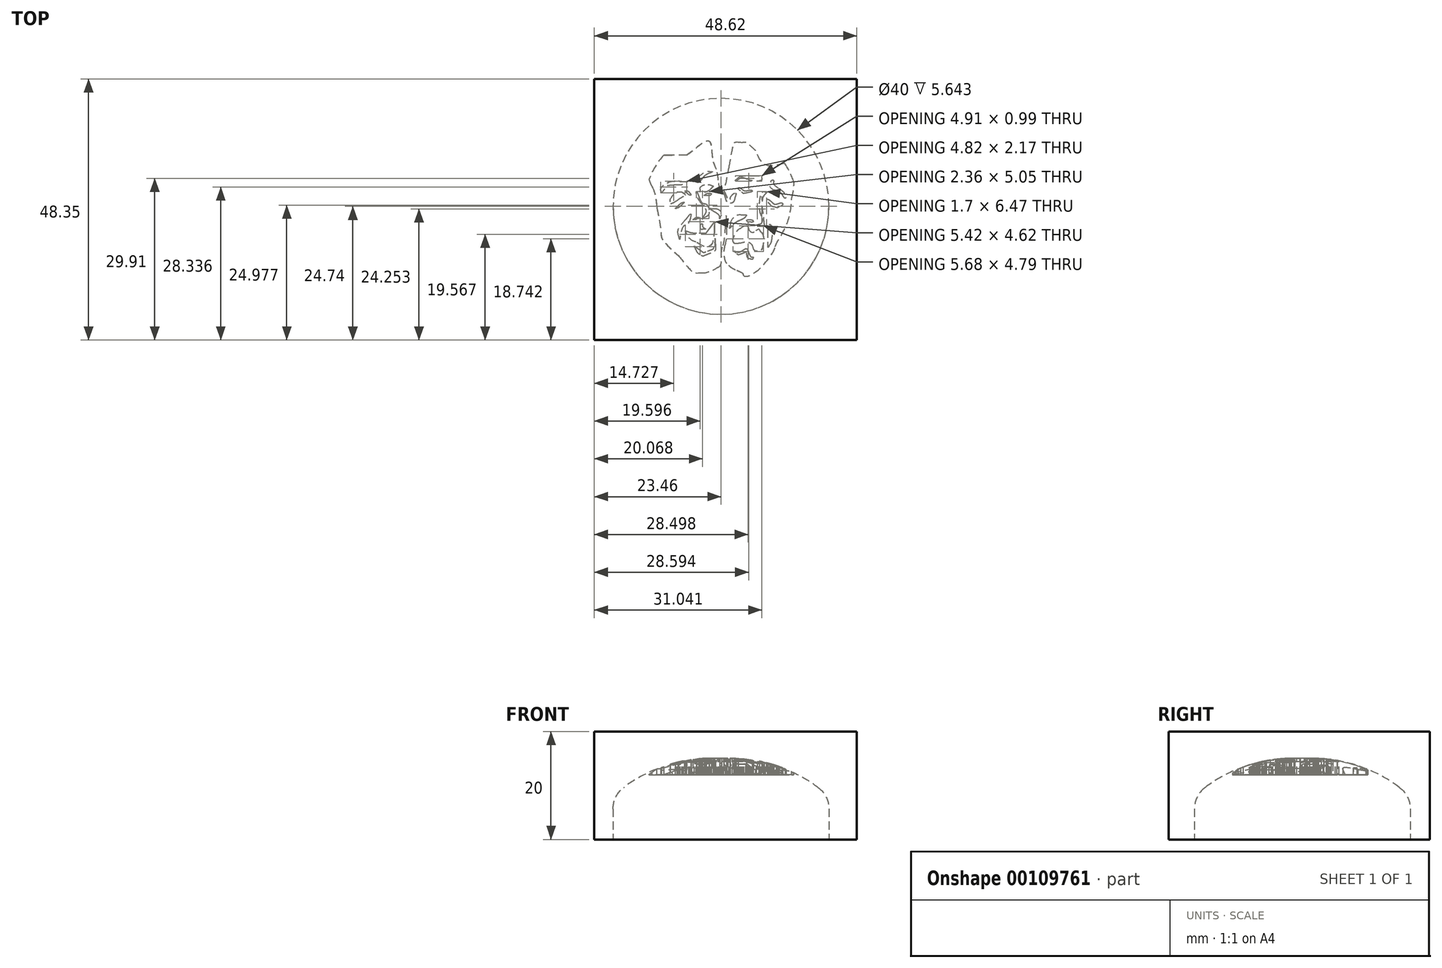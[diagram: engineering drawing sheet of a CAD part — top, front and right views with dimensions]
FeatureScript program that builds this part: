
annotation { "Feature Type Name" : "Feature", "Feature Type Description" : "" }
export const myFeature = defineFeature(function(context is Context, id is Id, definition is map)
    precondition{}
    {
        {
            var Q0;
            Q0=qCreatedBy(makeId("Front.planeOp"),FACE);
            var sketch = newSketch(context, id + "F0", { "sketchPlane" : qUnion([Q0])});
            skLineSegment(sketch, "E0", {"start": v(0, 0) * mm, "end": v(0, 15) * mm});
            skLineSegment(sketch, "E1", {"start": v(0, 0) * mm, "end": v(20, 0) * mm});
            skLineSegment(sketch, "E2", {"start": v(20, 0) * mm, "end": v(20, 8) * mm});
            skArc(sketch, "E3", {"start": v(20, 8) * mm, "mid": v(10.7, 13.52) * mm, "end": v(0, 15) * mm});
            skSolve(sketch);
        }
        {
            var Q0;
            Q0 = qSketchRegion(id + "F0", true);
            var Q1;
            Q1=sQuery(id+"F0.wireOp",EDGE,"E0");
            revolve(context, id + "F1", {"entities" : qUnion([Q0]), "axis" : qUnion([Q1]), "revolveType" : RevolveType.FULL});
        }
        {
            var Q0;
            Q0=makeQuery(id+"F1.opRevolve","SWEPT_EDGE",EDGE,{"disambiguationData":[OSD([sQuery(id+"F0.wireOp",EDGE,"E2"),sQuery(id+"F0.wireOp",EDGE,"E3")])]});
            fillet(context, id + "F2", {"entities" : qUnion([Q0]), "radius" : 5 * mm, "tangentPropagation" : true, "allowEdgeOverflow" : false});
        }
        {
            var Q0;
            Q0=qCreatedBy(makeId("Top.planeOp"),FACE);
            cPlane(context, id + "F3", {"entities" : qUnion([Q0]), "cplaneType" : CPlaneType.OFFSET, "offset" : 17 * mm, "width" : 150 * mm, "height" : 150 * mm});
        }
        {
            var Q0;
            Q0=qCreatedBy(id+"F3.planeOp",FACE);
            var sketch = newSketch(context, id + "F4", { "sketchPlane" : qUnion([Q0])});
            skFitSpline(sketch, "E4", {"points": [v(62.42, -44.87) * mm, v(62.37, -44.79) * mm, v(62.3, -44.69) * mm, v(62.25, -44.6) * mm]});
            skFitSpline(sketch, "E5", {"points": [v(62.25, -44.6) * mm, v(62.85, -45.92) * mm, v(62.76, -45.7) * mm, v(62.42, -44.87) * mm]});
            skFitSpline(sketch, "E6", {"points": [v(3.9, 11.8) * mm, v(2.5, 11.8) * mm, v(2.2, 11.26) * mm, v(1.52, 7.63) * mm]});
            skFitSpline(sketch, "E7", {"points": [v(1.52, 7.63) * mm, v(1.3, 6.43) * mm, v(0.74, 3.72) * mm, v(0.53, 2.94) * mm]});
            skFitSpline(sketch, "E8", {"points": [v(0.53, 2.94) * mm, v(0.9, 2.13) * mm, v(1.24, 1.06) * mm, v(1.13, 0.93) * mm]});
            skFitSpline(sketch, "E9", {"points": [v(1.13, 0.93) * mm, v(1.1, 0.88) * mm, v(0.97, 1.17) * mm, v(0.85, 1.57) * mm]});
            skFitSpline(sketch, "E10", {"points": [v(0.85, 1.57) * mm, v(0.73, 1.97) * mm, v(0.43, 2.56) * mm, v(0.17, 2.88) * mm]});
            skFitSpline(sketch, "E11", {"points": [v(0.17, 2.88) * mm, v(-0.15, 3.29) * mm, v(-0.35, 3.89) * mm, v(-0.48, 4.84) * mm]});
            skFitSpline(sketch, "E12", {"points": [v(-0.48, 4.84) * mm, v(-0.58, 5.6) * mm, v(-0.74, 6.48) * mm, v(-0.85, 6.8) * mm]});
            skFitSpline(sketch, "E13", {"points": [v(-0.85, 6.8) * mm, v(-1.55, 9.17) * mm, v(-2.14, 12.05) * mm, v(-5.37, 10.18) * mm]});
            skFitSpline(sketch, "E14", {"points": [v(-9.01, 9.45) * mm, v(-12.08, 9.45) * mm, v(-12.42, 9.31) * mm, v(-13, 7.85) * mm]});
            skFitSpline(sketch, "E15", {"points": [v(-13, 7.85) * mm, v(-13.5, 6.6) * mm, v(-13.4, 5.17) * mm, v(-12.73, 3.55) * mm]});
            skFitSpline(sketch, "E16", {"points": [v(-12.73, 3.55) * mm, v(-12.3, 2.53) * mm, v(-12.08, 1.56) * mm, v(-11.87, -0.27) * mm]});
            skFitSpline(sketch, "E17", {"points": [v(-11.87, -0.27) * mm, v(-11.13, -4.62) * mm, v(-10.9, -6) * mm, v(-7.88, -9.15) * mm]});
            skFitSpline(sketch, "E18", {"points": [v(-7.88, -9.15) * mm, v(-5.83, -11.6) * mm, v(-4.94, -12.28) * mm, v(-3.7, -12.28) * mm]});
            skFitSpline(sketch, "E19", {"points": [v(-3.7, -12.28) * mm, v(-2.98, -12.29) * mm, v(-1.58, -11.85) * mm, v(-0.72, -11.36) * mm]});
            skFitSpline(sketch, "E20", {"points": [v(-0.72, -11.36) * mm, v(-0.2, -11.05) * mm, v(0.09, -10.25) * mm, v(0.09, -9.05) * mm]});
            skFitSpline(sketch, "E21", {"points": [v(0.09, -9.05) * mm, v(0.09, -8.5) * mm, v(0.22, -7.69) * mm, v(0.37, -7.22) * mm]});
            skFitSpline(sketch, "E22", {"points": [v(0.37, -7.22) * mm, v(0.52, -6.76) * mm, v(0.72, -5.33) * mm, v(0.8, -4.04) * mm]});
            skLineSegment(sketch, "E23", {"start": v(-5.37, 10.18) * mm, "end": v(-6.32, 9.45) * mm});
            skLineSegment(sketch, "E24", {"start": v(-6.32, 9.45) * mm, "end": v(-9.01, 9.45) * mm});
            skFitSpline(sketch, "E25", {"points": [v(1, -3.74) * mm, v(1, -4.87) * mm, v(0.92, -6.3) * mm, v(0.8, -6.91) * mm]});
            skFitSpline(sketch, "E26", {"points": [v(0.8, -6.91) * mm, v(0.53, -8.32) * mm, v(0.84, -10.23) * mm, v(1.44, -10.9) * mm]});
            skFitSpline(sketch, "E27", {"points": [v(1.44, -10.9) * mm, v(1.67, -11.16) * mm, v(2.33, -11.58) * mm, v(2.92, -11.84) * mm]});
            skFitSpline(sketch, "E28", {"points": [v(2.92, -11.84) * mm, v(3.5, -12.1) * mm, v(4.03, -12.41) * mm, v(4.09, -12.53) * mm]});
            skFitSpline(sketch, "E29", {"points": [v(4.09, -12.53) * mm, v(4.27, -12.9) * mm, v(5.54, -12.75) * mm, v(6.16, -12.3) * mm]});
            skFitSpline(sketch, "E30", {"points": [v(6.16, -12.3) * mm, v(7.13, -11.59) * mm, v(9.66, -8.44) * mm, v(10.03, -7.49) * mm]});
            skFitSpline(sketch, "E31", {"points": [v(10.03, -7.49) * mm, v(10.22, -7) * mm, v(10.72, -6.04) * mm, v(11.16, -5.36) * mm]});
            skFitSpline(sketch, "E32", {"points": [v(11.16, -5.36) * mm, v(12.24, -3.17) * mm, v(12.87, -0.95) * mm, v(13.1, 1.48) * mm]});
            skFitSpline(sketch, "E33", {"points": [v(13.1, 1.48) * mm, v(13.3, 2.3) * mm, v(13.46, 3.37) * mm, v(13.46, 3.85) * mm]});
            skFitSpline(sketch, "E34", {"points": [v(13.46, 3.85) * mm, v(13.46, 4.33) * mm, v(13.55, 5.35) * mm, v(13.67, 6.13) * mm]});
            skFitSpline(sketch, "E35", {"points": [v(13.67, 6.13) * mm, v(13.95, 7.93) * mm, v(13.96, 8.1) * mm, v(12.64, 8.12) * mm]});
            skFitSpline(sketch, "E36", {"points": [v(12.64, 8.12) * mm, v(10.14, 7.62) * mm, v(8.09, 7.75) * mm, v(6.4, 10.34) * mm]});
            skFitSpline(sketch, "E37", {"points": [v(6.4, 10.34) * mm, v(5.04, 11.59) * mm, v(4.7, 11.8) * mm, v(3.9, 11.8) * mm]});
            skLineSegment(sketch, "E38", {"start": v(0.8, -4.04) * mm, "end": v(0.97, -1.7) * mm});
            skLineSegment(sketch, "E39", {"start": v(0.97, -1.7) * mm, "end": v(1, -3.74) * mm});
            skFitSpline(sketch, "E40", {"points": [v(-1.94, 6.43) * mm, v(-1.58, 6.42) * mm, v(-1.64, 6.36) * mm, v(-2.2, 6.11) * mm]});
            skFitSpline(sketch, "E41", {"points": [v(-2.2, 6.11) * mm, v(-2.6, 5.95) * mm, v(-3.15, 5.55) * mm, v(-3.42, 5.23) * mm]});
            skFitSpline(sketch, "E42", {"points": [v(-3.42, 5.23) * mm, v(-4.03, 4.54) * mm, v(-4.47, 4.45) * mm, v(-4.2, 5.08) * mm]});
            skFitSpline(sketch, "E43", {"points": [v(-4.2, 5.08) * mm, v(-3.96, 5.6) * mm, v(-2.55, 6.45) * mm, v(-1.94, 6.43) * mm]});
            skFitSpline(sketch, "E44", {"points": [v(5.6, 5.66) * mm, v(6.9, 5.66) * mm, v(7.52, 5.58) * mm, v(7.52, 5.4) * mm]});
            skFitSpline(sketch, "E45", {"points": [v(7.52, 5.4) * mm, v(7.52, 4.87) * mm, v(5.98, 4.72) * mm, v(4.65, 5.12) * mm]});
            skFitSpline(sketch, "E46", {"points": [v(4.65, 5.12) * mm, v(4, 5.32) * mm, v(3.75, 5.3) * mm, v(3.27, 5) * mm]});
            skFitSpline(sketch, "E47", {"points": [v(3.27, 5) * mm, v(2.95, 4.8) * mm, v(2.69, 4.7) * mm, v(2.69, 4.76) * mm]});
            skFitSpline(sketch, "E48", {"points": [v(2.69, 4.76) * mm, v(2.69, 4.82) * mm, v(2.92, 5.05) * mm, v(3.2, 5.27) * mm]});
            skFitSpline(sketch, "E49", {"points": [v(3.2, 5.27) * mm, v(3.6, 5.58) * mm, v(4.09, 5.66) * mm, v(5.6, 5.66) * mm]});
            skFitSpline(sketch, "E50", {"points": [v(9.52, 4.87) * mm, v(9.64, 4.88) * mm, v(9.75, 4.74) * mm, v(9.75, 4.45) * mm]});
            skFitSpline(sketch, "E51", {"points": [v(9.75, 4.45) * mm, v(9.75, 4.18) * mm, v(10.08, 3.78) * mm, v(10.66, 3.35) * mm]});
            skFitSpline(sketch, "E52", {"points": [v(10.66, 3.35) * mm, v(11.53, 2.7) * mm, v(12.07, 1.95) * mm, v(11.94, 1.56) * mm]});
            skFitSpline(sketch, "E53", {"points": [v(11.94, 1.56) * mm, v(11.9, 1.46) * mm, v(11.69, 1.66) * mm, v(11.45, 2.01) * mm]});
            skFitSpline(sketch, "E54", {"points": [v(11.45, 2.01) * mm, v(11.21, 2.36) * mm, v(10.68, 2.76) * mm, v(10.27, 2.9) * mm]});
            skFitSpline(sketch, "E55", {"points": [v(10.27, 2.9) * mm, v(9.49, 3.2) * mm, v(9.05, 3.9) * mm, v(9.25, 4.53) * mm]});
            skFitSpline(sketch, "E56", {"points": [v(9.25, 4.53) * mm, v(9.32, 4.74) * mm, v(9.42, 4.85) * mm, v(9.52, 4.87) * mm]});
            skFitSpline(sketch, "E57", {"points": [v(-7.88, 4.63) * mm, v(-7.8, 4.63) * mm, v(-7.7, 4.63) * mm, v(-7.62, 4.62) * mm]});
            skFitSpline(sketch, "E58", {"points": [v(-7.62, 4.62) * mm, v(-6.33, 4.5) * mm, v(-6.8, 4.1) * mm, v(-8.44, 3.96) * mm]});
            skFitSpline(sketch, "E59", {"points": [v(-8.44, 3.96) * mm, v(-9.9, 3.83) * mm, v(-10.05, 3.77) * mm, v(-10.53, 3.12) * mm]});
            skFitSpline(sketch, "E60", {"points": [v(-10.53, 3.12) * mm, v(-10.82, 2.73) * mm, v(-11.05, 2.5) * mm, v(-11.05, 2.62) * mm]});
            skFitSpline(sketch, "E61", {"points": [v(-11.05, 2.62) * mm, v(-11.05, 3.5) * mm, v(-9.24, 4.6) * mm, v(-7.88, 4.63) * mm]});
            skFitSpline(sketch, "E62", {"points": [v(-2.39, 3.99) * mm, v(-2.15, 4) * mm, v(-1.9, 3.95) * mm, v(-1.69, 3.85) * mm]});
            skFitSpline(sketch, "E63", {"points": [v(-1.69, 3.85) * mm, v(-1.44, 3.74) * mm, v(-1.46, 3.66) * mm, v(-1.81, 3.33) * mm]});
            skFitSpline(sketch, "E64", {"points": [v(-1.81, 3.33) * mm, v(-2.34, 2.84) * mm, v(-3.8, 2.57) * mm, v(-3.8, 2.97) * mm]});
            skFitSpline(sketch, "E65", {"points": [v(-3.8, 2.97) * mm, v(-3.8, 3.54) * mm, v(-3.1, 3.98) * mm, v(-2.39, 3.99) * mm]});
            skFitSpline(sketch, "E66", {"points": [v(3.37, 3.46) * mm, v(3.47, 3.46) * mm, v(3.65, 3.38) * mm, v(3.88, 3.2) * mm]});
            skFitSpline(sketch, "E67", {"points": [v(3.88, 3.2) * mm, v(4.21, 2.94) * mm, v(4.57, 2.85) * mm, v(5.01, 2.94) * mm]});
            skFitSpline(sketch, "E68", {"points": [v(5.01, 2.94) * mm, v(5.36, 3) * mm, v(5.7, 2.99) * mm, v(5.75, 2.89) * mm]});
            skFitSpline(sketch, "E69", {"points": [v(5.75, 2.89) * mm, v(5.8, 2.79) * mm, v(5.53, 2.64) * mm, v(5.14, 2.57) * mm]});
            skFitSpline(sketch, "E70", {"points": [v(5.14, 2.57) * mm, v(4.18, 2.38) * mm, v(4.14, 2.39) * mm, v(3.62, 2.86) * mm]});
            skFitSpline(sketch, "E71", {"points": [v(3.62, 2.86) * mm, v(3.25, 3.2) * mm, v(3.2, 3.45) * mm, v(3.37, 3.46) * mm]});
            skFitSpline(sketch, "E72", {"points": [v(-6.38, 2.87) * mm, v(-6.22, 2.87) * mm, v(-5.98, 2.72) * mm, v(-5.85, 2.54) * mm]});
            skFitSpline(sketch, "E73", {"points": [v(-5.85, 2.54) * mm, v(-5.56, 2.1) * mm, v(-5.86, 2.1) * mm, v(-6.33, 2.53) * mm]});
            skFitSpline(sketch, "E74", {"points": [v(-6.33, 2.53) * mm, v(-6.63, 2.8) * mm, v(-6.64, 2.86) * mm, v(-6.38, 2.87) * mm]});
            skFitSpline(sketch, "E75", {"points": [v(-4.54, 2.75) * mm, v(-4.5, 2.76) * mm, v(-4.32, 2.4) * mm, v(-4.1, 1.85) * mm]});
            skFitSpline(sketch, "E76", {"points": [v(-4.1, 1.85) * mm, v(-3.87, 1.22) * mm, v(-3.54, 0.65) * mm, v(-3.38, 0.58) * mm]});
            skFitSpline(sketch, "E77", {"points": [v(-3.38, 0.58) * mm, v(-2.5, 0.17) * mm, v(-2.3, -1.54) * mm, v(-3.1, -2.05) * mm]});
            skFitSpline(sketch, "E78", {"points": [v(-3.1, -2.05) * mm, v(-3.47, -2.3) * mm, v(-3.48, -2.29) * mm, v(-3.18, -1.78) * mm]});
            skFitSpline(sketch, "E79", {"points": [v(-3.18, -1.78) * mm, v(-2.74, -1.03) * mm, v(-2.8, -0.57) * mm, v(-3.5, 0.36) * mm]});
            skFitSpline(sketch, "E80", {"points": [v(-3.5, 0.36) * mm, v(-4.1, 1.2) * mm, v(-4.55, 2.2) * mm, v(-4.55, 2.72) * mm]});
            skFitSpline(sketch, "E81", {"points": [v(-4.55, 2.72) * mm, v(-4.55, 2.74) * mm, v(-4.55, 2.74) * mm, v(-4.54, 2.75) * mm]});
            skFitSpline(sketch, "E82", {"points": [v(-7.82, 2.65) * mm, v(-7.3, 2.65) * mm, v(-6.59, 2) * mm, v(-6.92, 1.83) * mm]});
            skFitSpline(sketch, "E83", {"points": [v(-6.92, 1.83) * mm, v(-7.05, 1.77) * mm, v(-7.54, 1.48) * mm, v(-8, 1.18) * mm]});
            skFitSpline(sketch, "E84", {"points": [v(-8, 1.18) * mm, v(-8.89, 0.61) * mm, v(-9.38, 0.5) * mm, v(-9.38, 0.86) * mm]});
            skFitSpline(sketch, "E85", {"points": [v(-9.38, 0.86) * mm, v(-9.38, 1.31) * mm, v(-8.21, 2.65) * mm, v(-7.82, 2.65) * mm]});
            skFitSpline(sketch, "E86", {"points": [v(8.28, 2.65) * mm, v(8.42, 2.65) * mm, v(8.39, 2.5) * mm, v(8.19, 2.24) * mm]});
            skFitSpline(sketch, "E87", {"points": [v(8.19, 2.24) * mm, v(7.77, 1.68) * mm, v(7.64, 0) * mm, v(7.85, -2.03) * mm]});
            skFitSpline(sketch, "E88", {"points": [v(7.85, -2.03) * mm, v(7.95, -2.95) * mm, v(8.02, -3.7) * mm, v(8, -3.72) * mm]});
            skFitSpline(sketch, "E89", {"points": [v(8, -3.72) * mm, v(8, -3.72) * mm, v(7.69, -3.67) * mm, v(7.33, -3.6) * mm]});
            skFitSpline(sketch, "E90", {"points": [v(7.33, -3.6) * mm, v(6.77, -3.48) * mm, v(6.73, -3.44) * mm, v(7.08, -3.3) * mm]});
            skFitSpline(sketch, "E91", {"points": [v(7.08, -3.3) * mm, v(7.54, -3.1) * mm, v(7.69, -2.6) * mm, v(7.5, -1.8) * mm]});
            skFitSpline(sketch, "E92", {"points": [v(7.5, -1.8) * mm, v(7.14, -0.28) * mm, v(7.65, 2.65) * mm, v(8.28, 2.65) * mm]});
            skFitSpline(sketch, "E93", {"points": [v(2.67, 2.43) * mm, v(2.71, 2.44) * mm, v(2.74, 2.43) * mm, v(2.76, 2.4) * mm]});
            skFitSpline(sketch, "E94", {"points": [v(2.76, 2.4) * mm, v(2.8, 2.36) * mm, v(2.7, 1.99) * mm, v(2.57, 1.6) * mm]});
            skFitSpline(sketch, "E95", {"points": [v(2.57, 1.6) * mm, v(2.3, 0.8) * mm, v(1.76, 0.6) * mm, v(1.76, 1.3) * mm]});
            skFitSpline(sketch, "E96", {"points": [v(1.76, 1.3) * mm, v(1.76, 1.65) * mm, v(2.4, 2.4) * mm, v(2.67, 2.43) * mm]});
            skFitSpline(sketch, "E97", {"points": [v(-2.18, 2.42) * mm, v(-1.95, 2.42) * mm, v(-1.79, 2.35) * mm, v(-1.86, 2.2) * mm]});
            skFitSpline(sketch, "E98", {"points": [v(-1.86, 2.2) * mm, v(-1.92, 2.08) * mm, v(-2.24, 1.98) * mm, v(-2.57, 1.99) * mm]});
            skFitSpline(sketch, "E99", {"points": [v(-2.57, 1.99) * mm, v(-3.02, 1.99) * mm, v(-3.1, 2.04) * mm, v(-2.88, 2.2) * mm]});
            skFitSpline(sketch, "E100", {"points": [v(-2.88, 2.2) * mm, v(-2.7, 2.35) * mm, v(-2.4, 2.42) * mm, v(-2.18, 2.42) * mm]});
            skFitSpline(sketch, "E101", {"points": [v(8.66, 1.31) * mm, v(8.75, 1.31) * mm, v(9.07, 1.1) * mm, v(9.37, 0.83) * mm]});
            skFitSpline(sketch, "E102", {"points": [v(9.37, 0.83) * mm, v(9.78, 0.47) * mm, v(10.07, 0.39) * mm, v(10.57, 0.48) * mm]});
            skFitSpline(sketch, "E103", {"points": [v(10.57, 0.48) * mm, v(11.28, 0.62) * mm, v(11.45, 0.35) * mm, v(10.87, -0.02) * mm]});
            skFitSpline(sketch, "E104", {"points": [v(10.87, -0.02) * mm, v(10.5, -0.26) * mm, v(10.43, -0.26) * mm, v(9.85, -0.09) * mm]});
            skFitSpline(sketch, "E105", {"points": [v(9.85, -0.09) * mm, v(9.46, 0.03) * mm, v(8.37, 1.31) * mm, v(8.66, 1.31) * mm]});
            skFitSpline(sketch, "E106", {"points": [v(-6.9, 0.76) * mm, v(-6.82, 0.75) * mm, v(-6.92, 0.61) * mm, v(-7.23, 0.31) * mm]});
            skFitSpline(sketch, "E107", {"points": [v(-7.23, 0.31) * mm, v(-7.53, 0.02) * mm, v(-7.94, -0.27) * mm, v(-8.15, -0.34) * mm]});
            skFitSpline(sketch, "E108", {"points": [v(-8.15, -0.34) * mm, v(-8.45, -0.43) * mm, v(-8.4, -0.33) * mm, v(-7.98, 0.08) * mm]});
            skFitSpline(sketch, "E109", {"points": [v(-7.98, 0.08) * mm, v(-7.68, 0.37) * mm, v(-7.26, 0.66) * mm, v(-7.06, 0.73) * mm]});
            skFitSpline(sketch, "E110", {"points": [v(-7.06, 0.73) * mm, v(-6.99, 0.75) * mm, v(-6.94, 0.76) * mm, v(-6.9, 0.76) * mm]});
            skFitSpline(sketch, "E111", {"points": [v(-1.92, -0.39) * mm, v(-1.8, -0.4) * mm, v(-1.61, -0.4) * mm, v(-1.41, -0.43) * mm]});
            skFitSpline(sketch, "E112", {"points": [v(-1.41, -0.43) * mm, v(-0.52, -0.53) * mm, v(0.12, -1.26) * mm, v(-0.1, -1.92) * mm]});
            skFitSpline(sketch, "E113", {"points": [v(-0.1, -1.92) * mm, v(-0.23, -2.3) * mm, v(-0.26, -2.3) * mm, v(-0.27, -1.98) * mm]});
            skFitSpline(sketch, "E114", {"points": [v(-0.27, -1.98) * mm, v(-0.28, -1.75) * mm, v(-0.65, -1.37) * mm, v(-1.21, -1.03) * mm]});
            skFitSpline(sketch, "E115", {"points": [v(-1.21, -1.03) * mm, v(-1.72, -0.72) * mm, v(-2.14, -0.44) * mm, v(-2.14, -0.4) * mm]});
            skFitSpline(sketch, "E116", {"points": [v(-2.14, -0.4) * mm, v(-2.14, -0.4) * mm, v(-2.06, -0.38) * mm, v(-1.92, -0.39) * mm]});
            skFitSpline(sketch, "E117", {"points": [v(-5.6, -1.42) * mm, v(-5.6, -1.42) * mm, v(-5.6, -1.42) * mm, v(-5.6, -1.42) * mm]});
            skFitSpline(sketch, "E118", {"points": [v(-5.6, -1.42) * mm, v(-5.55, -1.43) * mm, v(-5.56, -1.55) * mm, v(-5.6, -1.75) * mm]});
            skFitSpline(sketch, "E119", {"points": [v(-5.6, -1.75) * mm, v(-5.74, -2.47) * mm, v(-6.36, -3.6) * mm, v(-6.6, -3.6) * mm]});
            skFitSpline(sketch, "E120", {"points": [v(-6.6, -3.6) * mm, v(-6.86, -3.6) * mm, v(-7.37, -4.62) * mm, v(-7.52, -5.44) * mm]});
            skFitSpline(sketch, "E121", {"points": [v(-7.8, -5.54) * mm, v(-8, -4.65) * mm, v(-7.63, -3.78) * mm, v(-6.47, -2.36) * mm]});
            skFitSpline(sketch, "E122", {"points": [v(-6.47, -2.36) * mm, v(-5.95, -1.73) * mm, v(-5.7, -1.44) * mm, v(-5.6, -1.42) * mm]});
            skLineSegment(sketch, "E123", {"start": v(-7.52, -5.44) * mm, "end": v(-7.65, -6.16) * mm});
            skLineSegment(sketch, "E124", {"start": v(-7.65, -6.16) * mm, "end": v(-7.8, -5.54) * mm});
            skFitSpline(sketch, "E125", {"points": [v(4, -1.59) * mm, v(4.66, -1.59) * mm, v(4.74, -1.64) * mm, v(4.55, -1.9) * mm]});
            skFitSpline(sketch, "E126", {"points": [v(4.55, -1.9) * mm, v(4.43, -2.09) * mm, v(3.94, -2.4) * mm, v(3.46, -2.62) * mm]});
            skFitSpline(sketch, "E127", {"points": [v(3.46, -2.62) * mm, v(2.99, -2.83) * mm, v(2.36, -3.25) * mm, v(2.08, -3.56) * mm]});
            skLineSegment(sketch, "E128", {"start": v(-5.6, -1.42) * mm, "end": v(-5.6, -1.42) * mm});
            skFitSpline(sketch, "E129", {"points": [v(1.77, -3.43) * mm, v(2.07, -2.4) * mm, v(3.05, -1.59) * mm, v(4, -1.59) * mm]});
            skLineSegment(sketch, "E130", {"start": v(2.08, -3.56) * mm, "end": v(1.57, -4.13) * mm});
            skLineSegment(sketch, "E131", {"start": v(1.57, -4.13) * mm, "end": v(1.77, -3.43) * mm});
            skFitSpline(sketch, "E132", {"points": [v(-4.37, -2.04) * mm, v(-4.12, -2.04) * mm, v(-4.12, -2.07) * mm, v(-4.37, -2.26) * mm]});
            skFitSpline(sketch, "E133", {"points": [v(-4.37, -2.26) * mm, v(-4.52, -2.38) * mm, v(-4.77, -2.47) * mm, v(-4.92, -2.47) * mm]});
            skFitSpline(sketch, "E134", {"points": [v(-4.92, -2.47) * mm, v(-5.17, -2.47) * mm, v(-5.17, -2.45) * mm, v(-4.92, -2.26) * mm]});
            skFitSpline(sketch, "E135", {"points": [v(-4.92, -2.26) * mm, v(-4.77, -2.14) * mm, v(-4.52, -2.04) * mm, v(-4.37, -2.04) * mm]});
            skFitSpline(sketch, "E136", {"points": [v(5.27, -2.48) * mm, v(5.57, -2.48) * mm, v(5.87, -2.58) * mm, v(5.94, -2.7) * mm]});
            skFitSpline(sketch, "E137", {"points": [v(5.94, -2.7) * mm, v(6, -2.83) * mm, v(5.82, -2.92) * mm, v(5.5, -2.92) * mm]});
            skFitSpline(sketch, "E138", {"points": [v(5.5, -2.92) * mm, v(5.19, -2.92) * mm, v(4.89, -2.82) * mm, v(4.82, -2.7) * mm]});
            skFitSpline(sketch, "E139", {"points": [v(4.82, -2.7) * mm, v(4.76, -2.57) * mm, v(4.94, -2.48) * mm, v(5.27, -2.48) * mm]});
            skFitSpline(sketch, "E140", {"points": [v(-1.29, -4.05) * mm, v(-1.58, -6.74) * mm, v(-2.56, -7.5) * mm, v(-4.62, -6.61) * mm]});
            skFitSpline(sketch, "E141", {"points": [v(-4.62, -6.61) * mm, v(-5.35, -6.3) * mm, v(-6.12, -5.56) * mm, v(-6.42, -4.9) * mm]});
            skFitSpline(sketch, "E142", {"points": [v(-6.42, -4.9) * mm, v(-6.57, -4.56) * mm, v(-6.52, -4.54) * mm, v(-6, -4.72) * mm]});
            skFitSpline(sketch, "E143", {"points": [v(-6, -4.72) * mm, v(-5.66, -4.84) * mm, v(-4.8, -4.93) * mm, v(-4.07, -4.93) * mm]});
            skLineSegment(sketch, "E144", {"start": v(-1.16, -2.86) * mm, "end": v(-1.29, -4.05) * mm});
            skLineSegment(sketch, "E145", {"start": v(-1.29, -4.05) * mm, "end": v(-1.16, -2.86) * mm});
            skFitSpline(sketch, "E146", {"points": [v(-3.55, -3.23) * mm, v(-3.49, -3.24) * mm, v(-3.44, -3.32) * mm, v(-3.44, -3.46) * mm]});
            skFitSpline(sketch, "E147", {"points": [v(-3.44, -3.46) * mm, v(-3.44, -3.64) * mm, v(-3.3, -3.9) * mm, v(-3.11, -4.02) * mm]});
            skFitSpline(sketch, "E148", {"points": [v(-3.11, -4.02) * mm, v(-2.84, -4.22) * mm, v(-2.86, -4.25) * mm, v(-3.3, -4.26) * mm]});
            skFitSpline(sketch, "E149", {"points": [v(-3.3, -4.26) * mm, v(-3.68, -4.26) * mm, v(-3.8, -4.15) * mm, v(-3.8, -3.83) * mm]});
            skFitSpline(sketch, "E150", {"points": [v(-3.8, -3.83) * mm, v(-3.8, -3.6) * mm, v(-3.73, -3.33) * mm, v(-3.62, -3.26) * mm]});
            skFitSpline(sketch, "E151", {"points": [v(-3.62, -3.26) * mm, v(-3.6, -3.24) * mm, v(-3.57, -3.23) * mm, v(-3.55, -3.23) * mm]});
            skLineSegment(sketch, "E152", {"start": v(-4.07, -4.93) * mm, "end": v(-2.74, -4.93) * mm});
            skLineSegment(sketch, "E153", {"start": v(-2.74, -4.93) * mm, "end": v(-1.95, -3.9) * mm});
            skLineSegment(sketch, "E154", {"start": v(-1.95, -3.9) * mm, "end": v(-1.16, -2.86) * mm});
            skFitSpline(sketch, "E155", {"points": [v(8.87, -3.37) * mm, v(9.16, -3.37) * mm, v(9.5, -4.83) * mm, v(9.42, -5.72) * mm]});
            skFitSpline(sketch, "E156", {"points": [v(9.42, -5.72) * mm, v(9.38, -6.21) * mm, v(9.2, -6.84) * mm, v(9.03, -7.11) * mm]});
            skFitSpline(sketch, "E157", {"points": [v(9.03, -7.11) * mm, v(8.74, -7.58) * mm, v(8.72, -7.51) * mm, v(8.72, -5.49) * mm]});
            skFitSpline(sketch, "E158", {"points": [v(8.72, -5.49) * mm, v(8.72, -4.32) * mm, v(8.79, -3.37) * mm, v(8.87, -3.37) * mm]});
            skFitSpline(sketch, "E159", {"points": [v(4.57, -3.62) * mm, v(4.8, -3.61) * mm, v(4.97, -3.75) * mm, v(5.1, -4.02) * mm]});
            skFitSpline(sketch, "E160", {"points": [v(5.1, -4.02) * mm, v(5.36, -4.62) * mm, v(5.99, -4.81) * mm, v(6.54, -4.46) * mm]});
            skFitSpline(sketch, "E161", {"points": [v(6.54, -4.46) * mm, v(6.94, -4.2) * mm, v(7.03, -4.21) * mm, v(7.26, -4.59) * mm]});
            skFitSpline(sketch, "E162", {"points": [v(7.26, -4.59) * mm, v(7.83, -5.54) * mm, v(7.35, -8.28) * mm, v(6.6, -8.28) * mm]});
            skFitSpline(sketch, "E163", {"points": [v(6.6, -8.28) * mm, v(6.4, -8.28) * mm, v(6.14, -8.08) * mm, v(6.03, -7.83) * mm]});
            skFitSpline(sketch, "E164", {"points": [v(6.03, -7.83) * mm, v(5.67, -7.03) * mm, v(4.78, -6.65) * mm, v(3.6, -6.81) * mm]});
            skFitSpline(sketch, "E165", {"points": [v(3.6, -6.81) * mm, v(2.94, -6.9) * mm, v(2.5, -6.87) * mm, v(2.42, -6.73) * mm]});
            skFitSpline(sketch, "E166", {"points": [v(2.42, -6.73) * mm, v(2.2, -6.3) * mm, v(3.02, -4.51) * mm, v(3.65, -4.05) * mm]});
            skFitSpline(sketch, "E167", {"points": [v(3.65, -4.05) * mm, v(4.04, -3.76) * mm, v(4.34, -3.62) * mm, v(4.57, -3.62) * mm]});
            skFitSpline(sketch, "E168", {"points": [v(-1.04, -6.84) * mm, v(-1.02, -7.99) * mm, v(-1.28, -8.4) * mm, v(-2.32, -8.82) * mm]});
            skFitSpline(sketch, "E169", {"points": [v(-2.32, -8.82) * mm, v(-3.28, -9.21) * mm, v(-3.4, -9.22) * mm, v(-3.92, -8.91) * mm]});
            skFitSpline(sketch, "E170", {"points": [v(-3.92, -8.91) * mm, v(-4.13, -8.79) * mm, v(-4.45, -8.38) * mm, v(-4.64, -8.01) * mm]});
            skLineSegment(sketch, "E171", {"start": v(-1.07, -5.94) * mm, "end": v(-1.04, -6.84) * mm});
            skLineSegment(sketch, "E172", {"start": v(-1.04, -6.84) * mm, "end": v(-1.07, -5.94) * mm});
            skFitSpline(sketch, "E173", {"points": [v(-4.1, -7.95) * mm, v(-3.28, -8.52) * mm, v(-3.18, -8.55) * mm, v(-2.45, -8.27) * mm]});
            skFitSpline(sketch, "E174", {"points": [v(-2.45, -8.27) * mm, v(-1.45, -7.9) * mm, v(-1.37, -7.8) * mm, v(-1.2, -6.78) * mm]});
            skLineSegment(sketch, "E175", {"start": v(-4.64, -8.01) * mm, "end": v(-4.97, -7.33) * mm});
            skLineSegment(sketch, "E176", {"start": v(-4.97, -7.33) * mm, "end": v(-4.1, -7.95) * mm});
            skFitSpline(sketch, "E177", {"points": [v(4.6, -7.87) * mm, v(4.62, -7.87) * mm, v(4.64, -7.87) * mm, v(4.66, -7.87) * mm]});
            skFitSpline(sketch, "E178", {"points": [v(4.66, -7.87) * mm, v(4.85, -7.88) * mm, v(4.96, -8.11) * mm, v(5.16, -8.61) * mm]});
            skFitSpline(sketch, "E179", {"points": [v(5.16, -8.61) * mm, v(5.33, -9.04) * mm, v(5.6, -9.4) * mm, v(5.76, -9.4) * mm]});
            skFitSpline(sketch, "E180", {"points": [v(5.76, -9.4) * mm, v(5.92, -9.4) * mm, v(6, -9.5) * mm, v(5.94, -9.61) * mm]});
            skFitSpline(sketch, "E181", {"points": [v(5.94, -9.61) * mm, v(5.82, -9.85) * mm, v(5.78, -9.85) * mm, v(5.24, -9.68) * mm]});
            skFitSpline(sketch, "E182", {"points": [v(5.24, -9.68) * mm, v(5.06, -9.63) * mm, v(4.87, -9.33) * mm, v(4.8, -9.02) * mm]});
            skFitSpline(sketch, "E183", {"points": [v(4.8, -9.02) * mm, v(4.7, -8.58) * mm, v(4.6, -8.5) * mm, v(4.29, -8.6) * mm]});
            skFitSpline(sketch, "E184", {"points": [v(4.29, -8.6) * mm, v(3.38, -8.95) * mm, v(3.13, -8.96) * mm, v(2.78, -8.62) * mm]});
            skFitSpline(sketch, "E185", {"points": [v(2.78, -8.62) * mm, v(2.42, -8.28) * mm, v(2.43, -8.27) * mm, v(2.9, -8.4) * mm]});
            skFitSpline(sketch, "E186", {"points": [v(2.9, -8.4) * mm, v(3.2, -8.48) * mm, v(3.62, -8.4) * mm, v(3.96, -8.18) * mm]});
            skFitSpline(sketch, "E187", {"points": [v(3.96, -8.18) * mm, v(4.26, -8) * mm, v(4.45, -7.89) * mm, v(4.6, -7.87) * mm]});
            skLineSegment(sketch, "E188", {"start": v(-1.2, -6.78) * mm, "end": v(-1.07, -5.94) * mm});
            skLineSegment(sketch, "E189", {"start": v(-1.07, -5.94) * mm, "end": v(-1.07, -5.94) * mm});
            skLineSegment(sketch, "E190", {"start": v(-1.07, -5.94) * mm, "end": v(-1.2, -6.78) * mm});
            skSolve(sketch);
        }
        {
            var Q0;
            Q0 = qSketchRegion(id + "F4", true);
            extrude(context, id + "F5", {"entities" : qUnion([Q0]), "operationType" : NewBodyOperationType.REMOVE, "oppositeDirection" : true, "depth" : 5 * mm});
        }
        {
            var Q0;
            Q0=qCreatedBy(makeId("Top.planeOp"),FACE);
            var sketch = newSketch(context, id + "F6", { "sketchPlane" : qUnion([Q0])});
            skLineSegment(sketch, "E191.bottom", {"start": v(-23.46, 23.6) * mm, "end": v(25.16, 23.6) * mm});
            skLineSegment(sketch, "E191.top", {"start": v(-23.46, -24.74) * mm, "end": v(25.16, -24.74) * mm});
            skLineSegment(sketch, "E191.left", {"start": v(-23.46, 23.6) * mm, "end": v(-23.46, -24.74) * mm});
            skLineSegment(sketch, "E191.right", {"start": v(25.16, 23.6) * mm, "end": v(25.16, -24.74) * mm});
            skSolve(sketch);
        }
        {
            var Q0;
            Q0 = qSketchRegion(id + "F6", true);
            extrude(context, id + "F7", {"entities" : qUnion([Q0]), "depth" : 20 * mm});
        }
        {
            var Q0;
            Q0=makeQuery(id+"F1.opRevolve","SWEPT_BODY",BODY,{"disambiguationData":[OSD([sQuery(id+"F0.wireOp",EDGE,"E0"),sQuery(id+"F0.wireOp",EDGE,"E1"),sQuery(id+"F0.wireOp",EDGE,"E2"),sQuery(id+"F0.wireOp",EDGE,"E3")])]});
            var Q1;
            Q1=makeQuery(id+"F7.opExtrude","SWEPT_BODY",BODY,{"disambiguationData":[OSD([sQuery(id+"F6.wireOp",EDGE,"E191.bottom"),sQuery(id+"F6.wireOp",EDGE,"E191.top"),sQuery(id+"F6.wireOp",EDGE,"E191.left"),sQuery(id+"F6.wireOp",EDGE,"E191.right")])]});
            booleanBodies(context, id + "F8", {"operationType" : BooleanOperationType.SUBTRACTION, "tools" : qUnion([Q0]), "targets" : qUnion([Q1]), "keepTools" : true});
        }
    });
